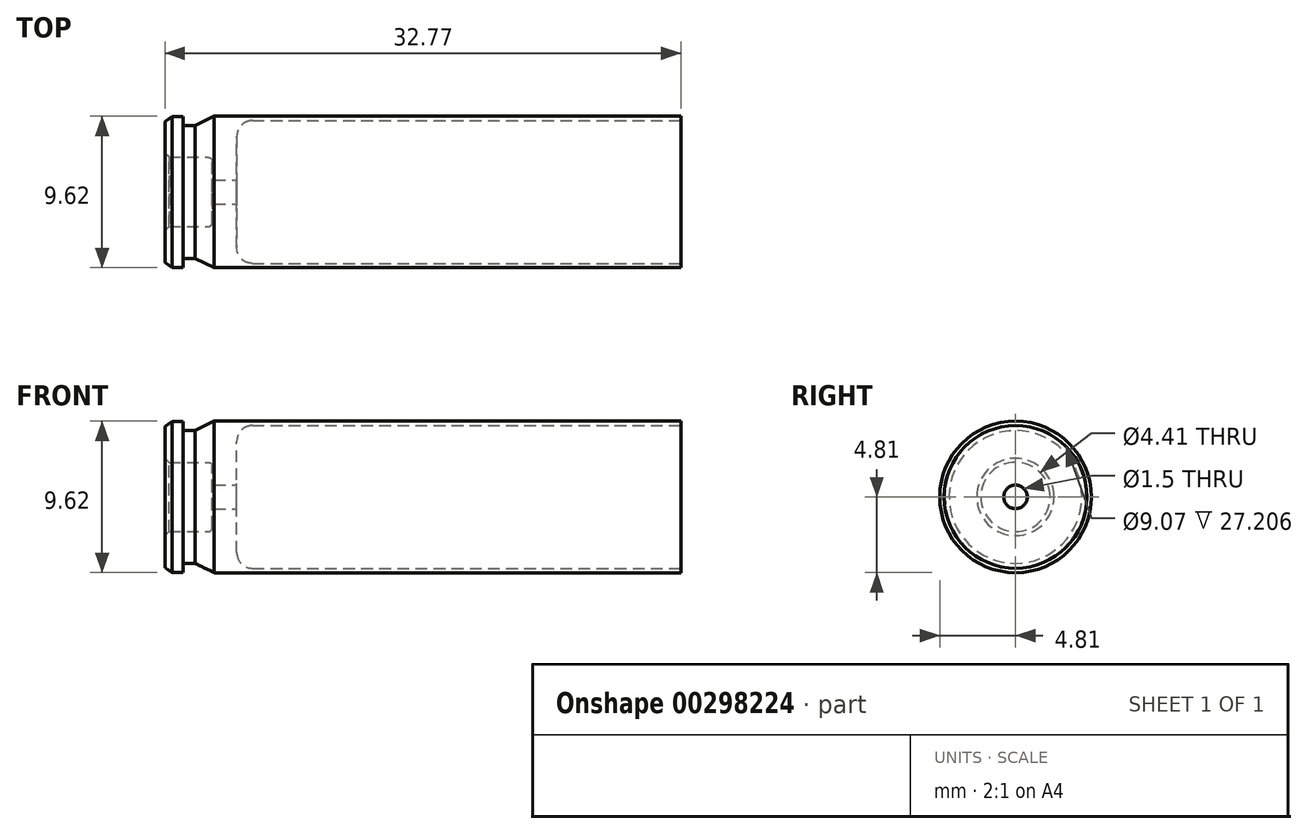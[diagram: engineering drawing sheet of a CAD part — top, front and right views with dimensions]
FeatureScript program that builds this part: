
annotation { "Feature Type Name" : "Feature", "Feature Type Description" : "" }
export const myFeature = defineFeature(function(context is Context, id is Id, definition is map)
    precondition{}
    {
        {
            var Q0;
            Q0=qCreatedBy(makeId("Top.planeOp"),FACE);
            var sketch = newSketch(context, id + "F0", { "sketchPlane" : qUnion([Q0])});
            skLineSegment(sketch, "E0", {"start": v(0, 2.2) * mm, "end": v(0, 4.48) * mm});
            skLineSegment(sketch, "E1", {"start": v(0, 4.48) * mm, "end": v(0.45, 4.8) * mm});
            skLineSegment(sketch, "E2", {"start": v(0.45, 4.8) * mm, "end": v(1.14, 4.8) * mm});
            skLineSegment(sketch, "E3", {"start": v(1.14, 4.8) * mm, "end": v(1.14, 4.21) * mm});
            skLineSegment(sketch, "E4", {"start": v(1.14, 4.21) * mm, "end": v(1.9, 4.22) * mm});
            skLineSegment(sketch, "E5", {"start": v(1.9, 4.21) * mm, "end": v(3.13, 4.81) * mm});
            skLineSegment(sketch, "E6", {"start": v(3.13, 4.81) * mm, "end": v(32.77, 4.81) * mm});
            skLineSegment(sketch, "E7", {"start": v(32.77, 4.81) * mm, "end": v(32.77, 4.53) * mm});
            skLineSegment(sketch, "E8", {"start": v(32.77, 0) * mm, "end": v(0, 0) * mm});
            skLineSegment(sketch, "E9.0", {"start": v(5.56, 4.53) * mm, "end": v(32.77, 4.53) * mm});
            skLineSegment(sketch, "E10", {"start": v(4.56, 3.53) * mm, "end": v(4.56, 0.85) * mm});
            skPoint(sketch, "E11.visualSharp", {"position": v(4.56, 4.53) * mm});
            skArc(sketch, "E11.filletArc", {"start": v(5.56, 4.53) * mm, "mid": v(4.85, 4.24) * mm, "end": v(4.56, 3.53) * mm});
            skLineSegment(sketch, "E12", {"start": v(0, 2.2) * mm, "end": v(2.75, 2.2) * mm});
            skLineSegment(sketch, "E13", {"start": v(3, 1.96) * mm, "end": v(3, 0.85) * mm});
            skLineSegment(sketch, "E14", {"start": v(3.1, 0.75) * mm, "end": v(4.46, 0.75) * mm});
            skPoint(sketch, "E15.visualSharp", {"position": v(3, 0.75) * mm});
            skArc(sketch, "E15.filletArc", {"start": v(3, 0.85) * mm, "mid": v(3.03, 0.78) * mm, "end": v(3.1, 0.75) * mm});
            skPoint(sketch, "E16.newPointB", {"position": v(4.56, 0) * mm});
            skArc(sketch, "E16.filletArc", {"start": v(4.46, 0.75) * mm, "mid": v(4.53, 0.78) * mm, "end": v(4.56, 0.85) * mm});
            skPoint(sketch, "E17.visualSharp", {"position": v(3, 2.2) * mm});
            skArc(sketch, "E17.filletArc", {"start": v(3, 1.96) * mm, "mid": v(2.93, 2.13) * mm, "end": v(2.75, 2.2) * mm});
            skSolve(sketch);
        }
        {
            var Q0;
            Q0=makeQuery(id+"F0.imprint","IMPRINT",FACE,{"disambiguationData":[TD([[makeQuery(id+"F0.imprint","IMPRINT",EDGE,{"derivedFrom":sQuery(id+"F0.wireOp",EDGE,"E0")}),-1.0]])]});
            var Q1;
            Q1=sQuery(id+"F0.wireOp",EDGE,"E8");
            revolve(context, id + "F1", {"entities" : qUnion([Q0]), "axis" : qUnion([Q1]), "revolveType" : RevolveType.FULL});
        }
        {
            var Q0;
            Q0=makeQuery(id+"F1.opRevolve","SWEPT_EDGE",EDGE,{"disambiguationData":[OSD([sQuery(id+"F0.wireOp",EDGE,"E0"),sQuery(id+"F0.wireOp",EDGE,"E12")])]});
            chamfer(context, id + "F2", {"entities" : qUnion([Q0]), "width" : .25 * mm, "tangentPropagation" : true});
        }
    });
